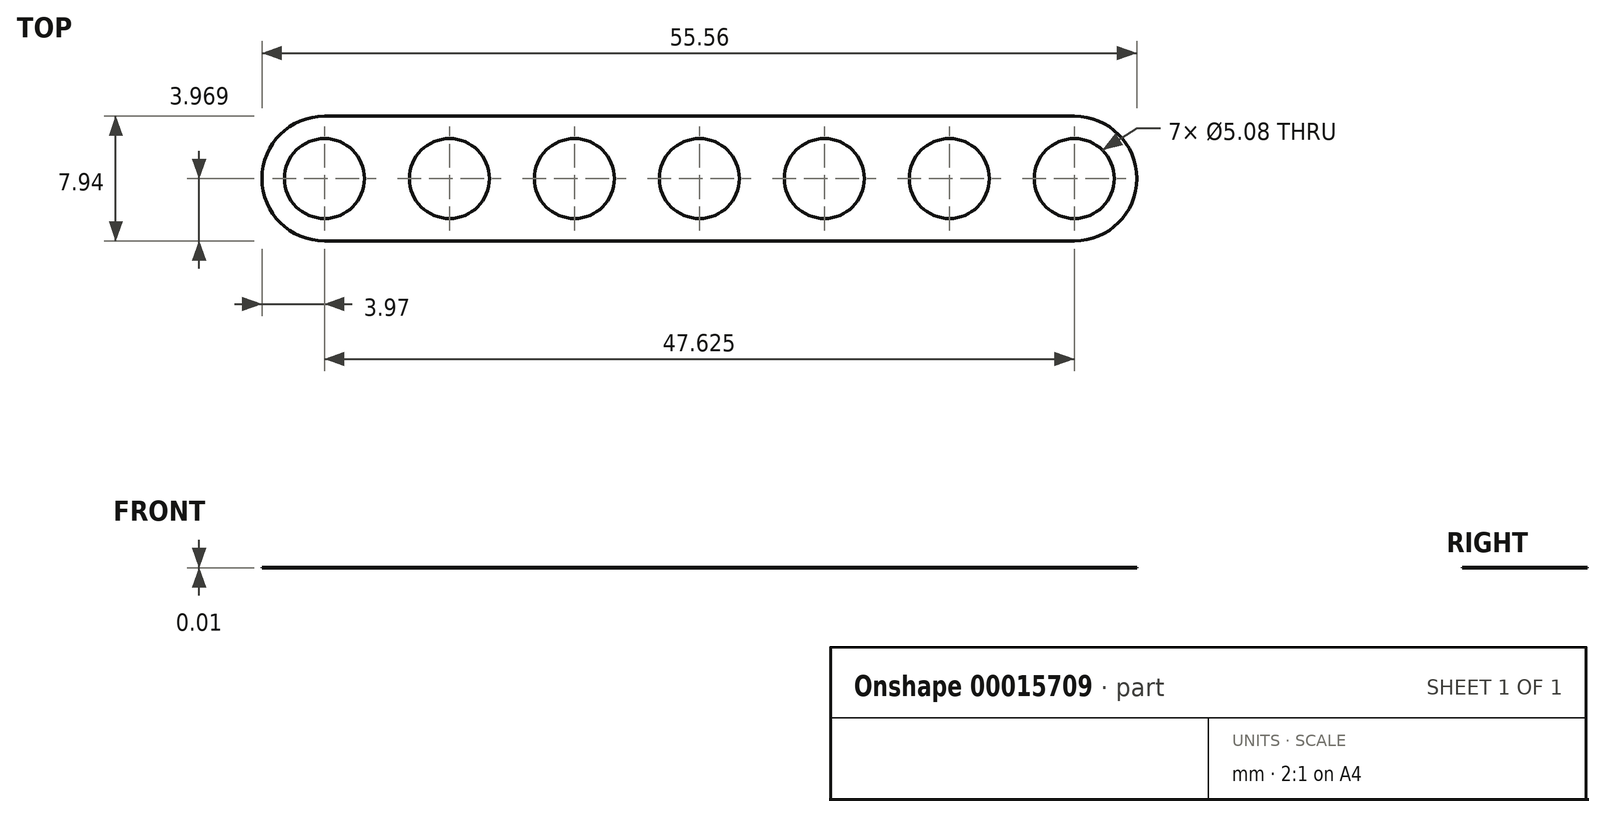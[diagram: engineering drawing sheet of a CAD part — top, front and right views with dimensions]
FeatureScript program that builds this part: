
annotation { "Feature Type Name" : "Feature", "Feature Type Description" : "" }
export const myFeature = defineFeature(function(context is Context, id is Id, definition is map)
    precondition{}
    {
        {
            var Q0;
            Q0=qCreatedBy(makeId("Top.planeOp"),FACE);
            var sketch = newSketch(context, id + "F0", { "sketchPlane" : qUnion([Q0])});
            skLineSegment(sketch, "E0.bottom", {"start": v(0, 0) * mm, "end": v(47.62, 0) * mm});
            skLineSegment(sketch, "E0.top", {"start": v(0, 7.94) * mm, "end": v(47.62, 7.94) * mm});
            skLineSegment(sketch, "E0.left", {"start": v(0, 0) * mm, "end": v(0, 7.94) * mm});
            skLineSegment(sketch, "E0.right", {"start": v(47.62, 0) * mm, "end": v(47.62, 7.94) * mm});
            skCircle(sketch, "E1", {"center": v(47.62, 3.97) * mm, "radius": 2.54 * mm});
            skCircle(sketch, "E2", {"center": v(0, 3.97) * mm, "radius": 2.54 * mm});
            skLineSegment(sketch, "E3", {"start": v(7.94, 3.97) * mm, "end": v(0, 3.97) * mm});
            skArc(sketch, "E4", {"start": v(47.62, 0) * mm, "mid": v(51.6, 3.97) * mm, "end": v(47.62, 7.94) * mm});
            skArc(sketch, "E5", {"start": v(0, 7.94) * mm, "mid": v(-3.97, 3.97) * mm, "end": v(0, 0) * mm});
            skLineSegment(sketch, "E6", {"start": v(7.94, 3.97) * mm, "end": v(15.88, 3.97) * mm});
            skLineSegment(sketch, "E7", {"start": v(15.88, 3.97) * mm, "end": v(23.81, 3.97) * mm});
            skLineSegment(sketch, "E8", {"start": v(23.81, 3.97) * mm, "end": v(31.75, 3.97) * mm});
            skLineSegment(sketch, "E9", {"start": v(31.75, 3.97) * mm, "end": v(39.69, 3.97) * mm});
            skLineSegment(sketch, "E10", {"start": v(39.69, 3.97) * mm, "end": v(47.62, 3.97) * mm});
            skCircle(sketch, "E11", {"center": v(7.94, 3.97) * mm, "radius": 2.54 * mm});
            skCircle(sketch, "E12", {"center": v(15.88, 3.97) * mm, "radius": 2.54 * mm});
            skCircle(sketch, "E13", {"center": v(23.81, 3.97) * mm, "radius": 2.54 * mm});
            skCircle(sketch, "E14", {"center": v(31.75, 3.97) * mm, "radius": 2.54 * mm});
            skCircle(sketch, "E15", {"center": v(39.69, 3.97) * mm, "radius": 2.54 * mm});
            skSolve(sketch);
        }
        {
            var Q0;
            Q0=qSketchRegion(id+"F0",true);
            extrude(context, id + "F1", {"entities" : qUnion([Q0]), "depth" : 5 / 406.4 * mm});
        }
    });
